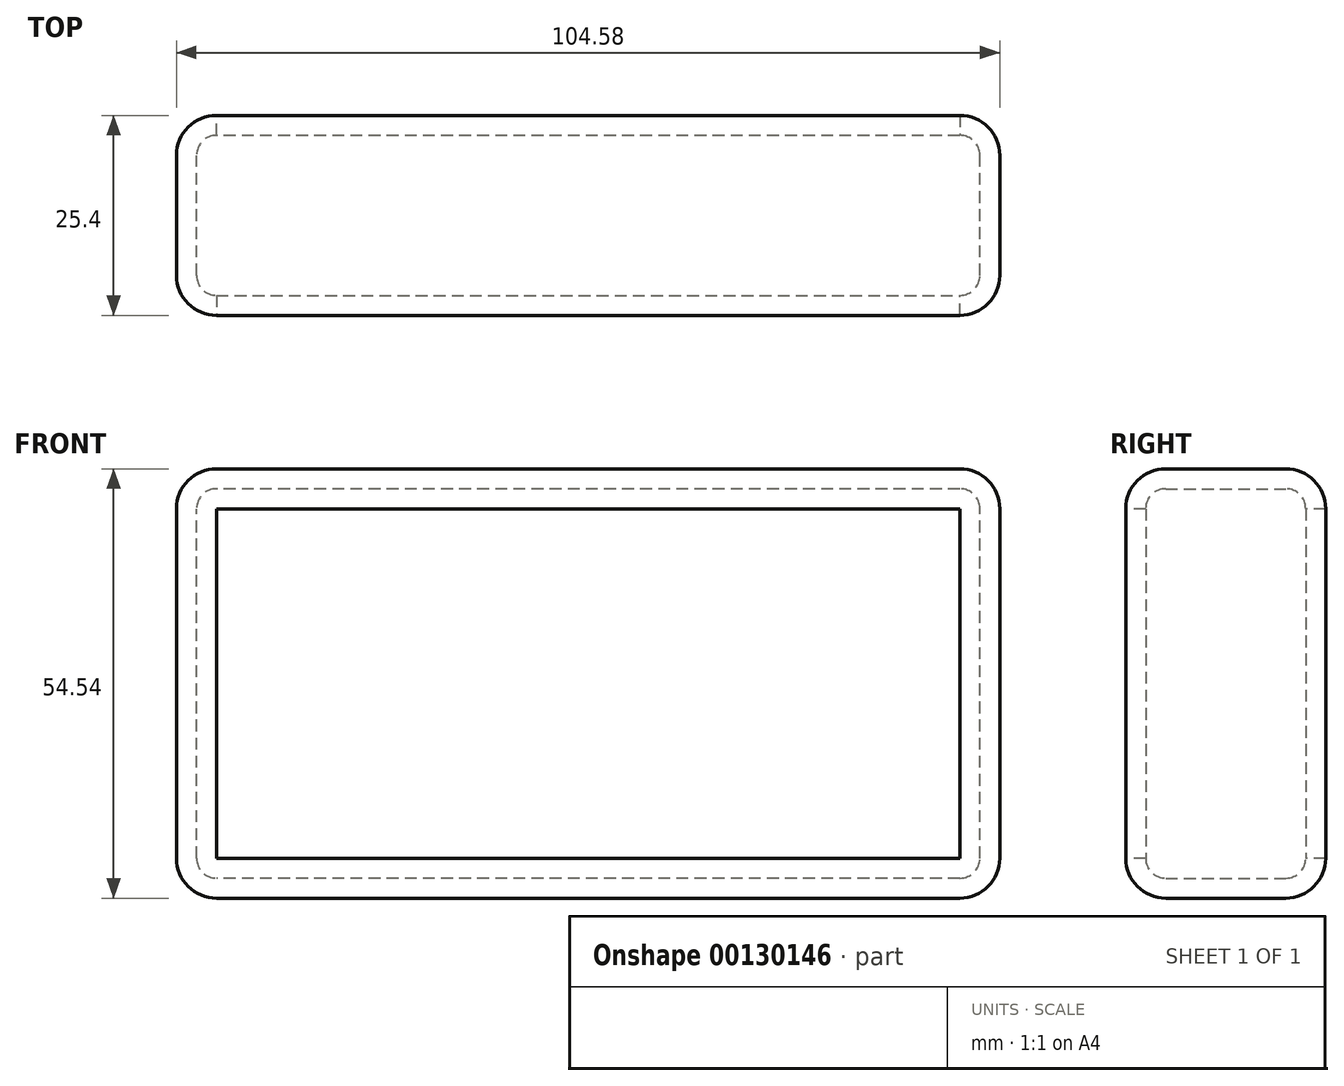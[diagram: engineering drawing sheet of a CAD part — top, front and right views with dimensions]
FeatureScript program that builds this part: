
annotation { "Feature Type Name" : "Feature", "Feature Type Description" : "" }
export const myFeature = defineFeature(function(context is Context, id is Id, definition is map)
    precondition{}
    {
        {
            var Q0;
            Q0=qCreatedBy(makeId("Front.planeOp"),FACE);
            var sketch = newSketch(context, id + "F0", { "sketchPlane" : qUnion([Q0])});
            skLineSegment(sketch, "E0.bottom", {"start": v(52.3, -27.27) * mm, "end": v(-52.3, -27.27) * mm});
            skLineSegment(sketch, "E0.top", {"start": v(52.3, 27.27) * mm, "end": v(-52.3, 27.27) * mm});
            skLineSegment(sketch, "E0.left", {"start": v(52.3, -27.27) * mm, "end": v(52.3, 27.27) * mm});
            skLineSegment(sketch, "E0.right", {"start": v(-52.3, -27.27) * mm, "end": v(-52.3, 27.27) * mm});
            skPoint(sketch, "E0.middle", {"position": v(0, 0) * mm});
            skSolve(sketch);
        }
        {
            var Q0;
            Q0=makeQuery(id+"F0.imprint","IMPRINT",FACE,{"disambiguationData":[TD([[makeQuery(id+"F0.imprint","IMPRINT",EDGE,{"derivedFrom":sQuery(id+"F0.wireOp",EDGE,"E0.bottom")}),-1.0]])]});
            extrude(context, id + "F1", {"entities" : qUnion([Q0]), "endBound" : BoundingType.SYMMETRIC, "depth" : 25.4 * mm});
        }
        {
            var Q0;
            Q0=makeQuery(id+"F1.opExtrude","SWEPT_FACE",FACE,{"disambiguationData":[OSD([sQuery(id+"F0.wireOp",EDGE,"E0.top")])]});
            var Q1;
            Q1=makeQuery(id+"F1.opExtrude","SWEPT_FACE",FACE,{"disambiguationData":[OSD([sQuery(id+"F0.wireOp",EDGE,"E0.left")])]});
            fillet(context, id + "F2", {"entities" : qUnion([Q0, Q1]), "radius" : 5.08 * mm, "tangentPropagation" : true, "allowEdgeOverflow" : false});
        }
        {
            var Q0;
            Q0=makeQuery(id+"F1.opExtrude","SWEPT_FACE",FACE,{"disambiguationData":[OSD([sQuery(id+"F0.wireOp",EDGE,"E0.right")])]});
            var Q1;
            Q1=makeQuery(id+"F1.opExtrude","SWEPT_FACE",FACE,{"disambiguationData":[OSD([sQuery(id+"F0.wireOp",EDGE,"E0.bottom")])]});
            fillet(context, id + "F3", {"entities" : qUnion([Q0, Q1]), "radius" : 5.08 * mm, "tangentPropagation" : true, "allowEdgeOverflow" : false});
        }
        {
            var Q0;
            Q0=makeQuery(id+"F1.opExtrude","CAP_FACE",FACE,{"disambiguationData":[OSD([sQuery(id+"F0.wireOp",EDGE,"E0.bottom"),sQuery(id+"F0.wireOp",EDGE,"E0.top"),sQuery(id+"F0.wireOp",EDGE,"E0.left"),sQuery(id+"F0.wireOp",EDGE,"E0.right")])],"isStart":false});
            var Q1;
            Q1=makeQuery(id+"F1.opExtrude","CAP_FACE",FACE,{"disambiguationData":[OSD([sQuery(id+"F0.wireOp",EDGE,"E0.bottom"),sQuery(id+"F0.wireOp",EDGE,"E0.top"),sQuery(id+"F0.wireOp",EDGE,"E0.left"),sQuery(id+"F0.wireOp",EDGE,"E0.right")])],"isStart":true});
            shell(context, id + "F4", {"entities" : qUnion([Q0, Q1]), "thickness" : 2.54 * mm});
        }
    });
